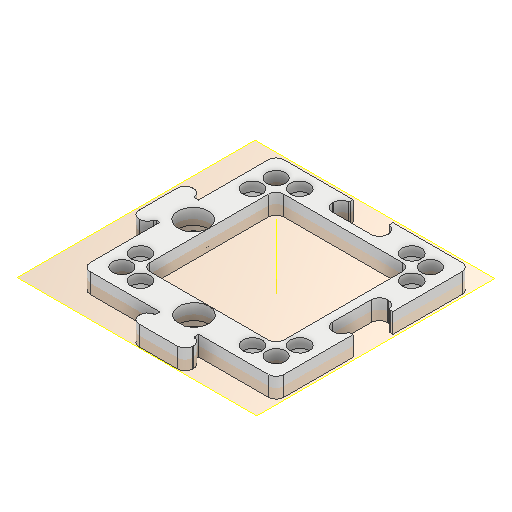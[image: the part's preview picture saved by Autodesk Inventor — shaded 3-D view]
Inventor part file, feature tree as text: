
AUTODESK INVENTOR PART (.ipt)
format: ipt  version: 2022 (Build 260153000, 153)  size: 502,272 bytes
history: native  units: mm
features: sketch x6, extrude x4, projected_geometry x4, mirror x2, pattern_circular x2, other x1, hole x1, plane x1
ambient origin geometry x8: Origin, YZ Plane, XZ Plane, XY Plane, X Axis, Y Axis, Z Axis, Center Point
bodies: Volumenkörper1 (feature_tree)
feature tree (21):
  extrude  "Extrusion1"  TaperAngle=0.0deg  [1 undecoded]
  mirror  "Mirror6"
  mirror  "Mirror7"
  extrude  "Extrusion13"  TaperAngle=0.0deg  [1 undecoded]
  sketch  "Sketch27"  dims[d9=0.0mm d13=0.0mm]
  extrude  "Extrusion14"  TaperAngle=0.0deg  [1 undecoded]
  other  "Work Axis4"
  pattern_circular  "Circular Pattern6"  [2 undecoded]
  hole  "Hole7"  [1 undecoded]
  pattern_circular  "Circular Pattern7"  [2 undecoded]
  plane  "Work Plane14"
  extrude  "Extrusion16"  Depth=0.3mm
  sketch  "Skizze1"  dims[d5=0.0mm d6=0.0mm]
  sketch  "Sketch26"  dims[d7=0.0mm d8=0.0mm]
  projected_geometry  "Projected Loop21"
  projected_geometry  "Projected Loop22"
  sketch  "Sketch28"  dims[d14=0.0mm]
  projected_geometry  "Projected Loop23"
  sketch  "Sketch29"  dims[d20=0.0mm]
  projected_geometry  "Projected Loop24"
  sketch  "Sketch32"  dims[d21=0.0mm d22=0.0mm d23=0.0mm d24=0.0mm d25=3.0mm d26=0.0mm d27=0.0mm d28=0.0mm d29=0.0mm d30=0.0mm d31=0.0mm d32=0.0mm d33=0.0mm d34=0.0mm d46=0.0mm d47=0.0mm d48=0.0mm d49=-10.0mm d50=0.0mm d51=0.0mm d52=0.0mm d53=0.0mm d54=0.0mm d55=0.0mm d56=0.0mm d57=0.0mm d58=0.0mm d59=0.0mm d77=2.65mm d82=2.65mm d222=0.5mm d236=5.3mm d278=25.0mm d279=25.0mm d2=7.7mm d281=7.7mm d282=2.0mm d283=4.8mm d286=4.9mm d292=2.0mm d293=5.4mm d298=10.0mm d299=0.0mm d300=2.0mm d301=0.5mm d302=10.0mm d303=0.0mm d308=20.0mm d309=90.0deg d319=7.78mm d320=4.0mm d321=21.4mm d322=4.0mm d323=4.3mm d324=6.0mm d325=7.8mm d326=4.0mm d327=90.0deg d328=8.0mm d329=20.594885mm d348=20.0mm d349=90.0deg d351=5.1mm d352=5.1mm d353=4.45mm d354=4.45mm d355=10.55mm d356=10.55mm d358=5.0mm d359=4.1mm d371=6.94mm d372=0.2mm d373=2.2mm d374=13.9mm d375=0.1mm d376=0.3mm d377=0.0mm]
note: 8 required parameter values undecoded (feature->parameter linkage not recoverable at this tier; creation-order binding heuristic only, values carry confidence <= 0.55)
